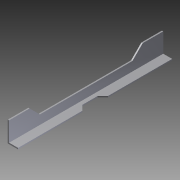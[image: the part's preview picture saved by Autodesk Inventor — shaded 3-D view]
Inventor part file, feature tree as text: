
AUTODESK INVENTOR PART (.ipt)
format: ipt  version: 2012 (Build 160160000, 160)  size: 103,424 bytes
history: native  units: in
note: dims shown in document units (in); Inventor stores cm internally (conversion verified against a paired STEP export)
features: extrude x3, sketch x3
ambient origin geometry x8: Origin, YZ Plane, XZ Plane, XY Plane, X Axis, Y Axis, Z Axis, Center Point
bodies: Solid1 (feature_tree)
feature tree (6):
  extrude  "Extrusion1"  Depth=0.9996in
  extrude  "Extrusion2"  Depth=0.125in
  extrude  "Extrusion3"  Depth=0.5in
  sketch  "Sketch1"  dims[d0=2.0095in d1=0.9996in]
  sketch  "Sketch2"  dims[d2=0.125in d3=0.125in]
  sketch  "Sketch3"  dims[d4=15.0in d5=0.0in d6=0.5in d7=45.0deg d8=45.0deg d9=1.5in d10=6.75in d11=12.0in d12=0.0in d13=1.0in d14=45.0deg d15=45.0deg d16=2.0in d17=2.0in d18=12.0in d19=0.0in]
